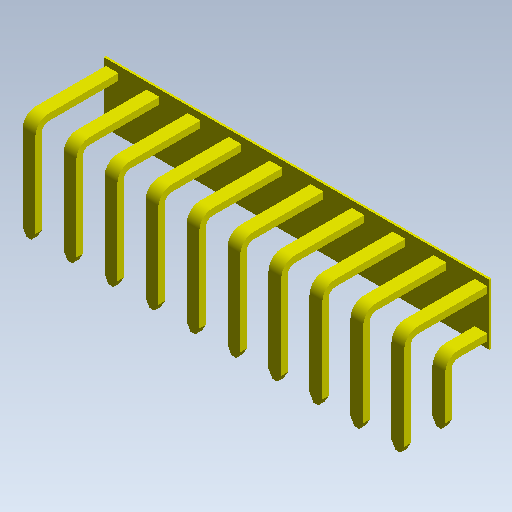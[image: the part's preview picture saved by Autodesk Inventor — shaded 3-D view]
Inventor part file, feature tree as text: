
AUTODESK INVENTOR PART (.ipt)
format: ipt  version: 2021 (Build 250183000, 183)  size: 389,632 bytes
history: native  units: mm (DEFAULTED — no unit token found)
features: other x7, extrude x5, sketch x5
ambient origin geometry x8: Origin, YZ Plane, XZ Plane, XY Plane, X Axis, Y Axis, Z Axis, Center Point
bodies: Solid1 (feature_tree)
feature tree (17):
  extrude  "Extrusion1"  Depth=23.9014mm TaperAngle=0.0deg
  extrude  "Extrusion2"  Depth=23.9014mm TaperAngle=0.0deg
  extrude  "Extrusion3"  [1 undecoded]
  extrude  "Extrusion4"  [1 undecoded]
  extrude  "Extrusion5"  [1 undecoded]
  other  "pin_XY"
  other  "pin_YZ"
  other  "pin_ZX"
  other  "pin_X"
  other  "pin_Y"
  other  "pin_Z"
  other  "pin_Center"
  sketch  "Sketch_13"
  sketch  "Sketch_12"  dims[d8=50.8mm d9=0.0mm]
  sketch  "Sketch_14"
  sketch  "Sketch_8"  dims[d0=0.127mm d1=0.0mm d2=23.9014mm d3=0.0mm]
  sketch  "Sketch_11"  dims[d4=23.9014mm d5=0.0mm d6=50.8mm d7=0.0mm]
note: 3 required parameter values undecoded (feature->parameter linkage not recoverable at this tier; creation-order binding heuristic only, values carry confidence <= 0.55)
